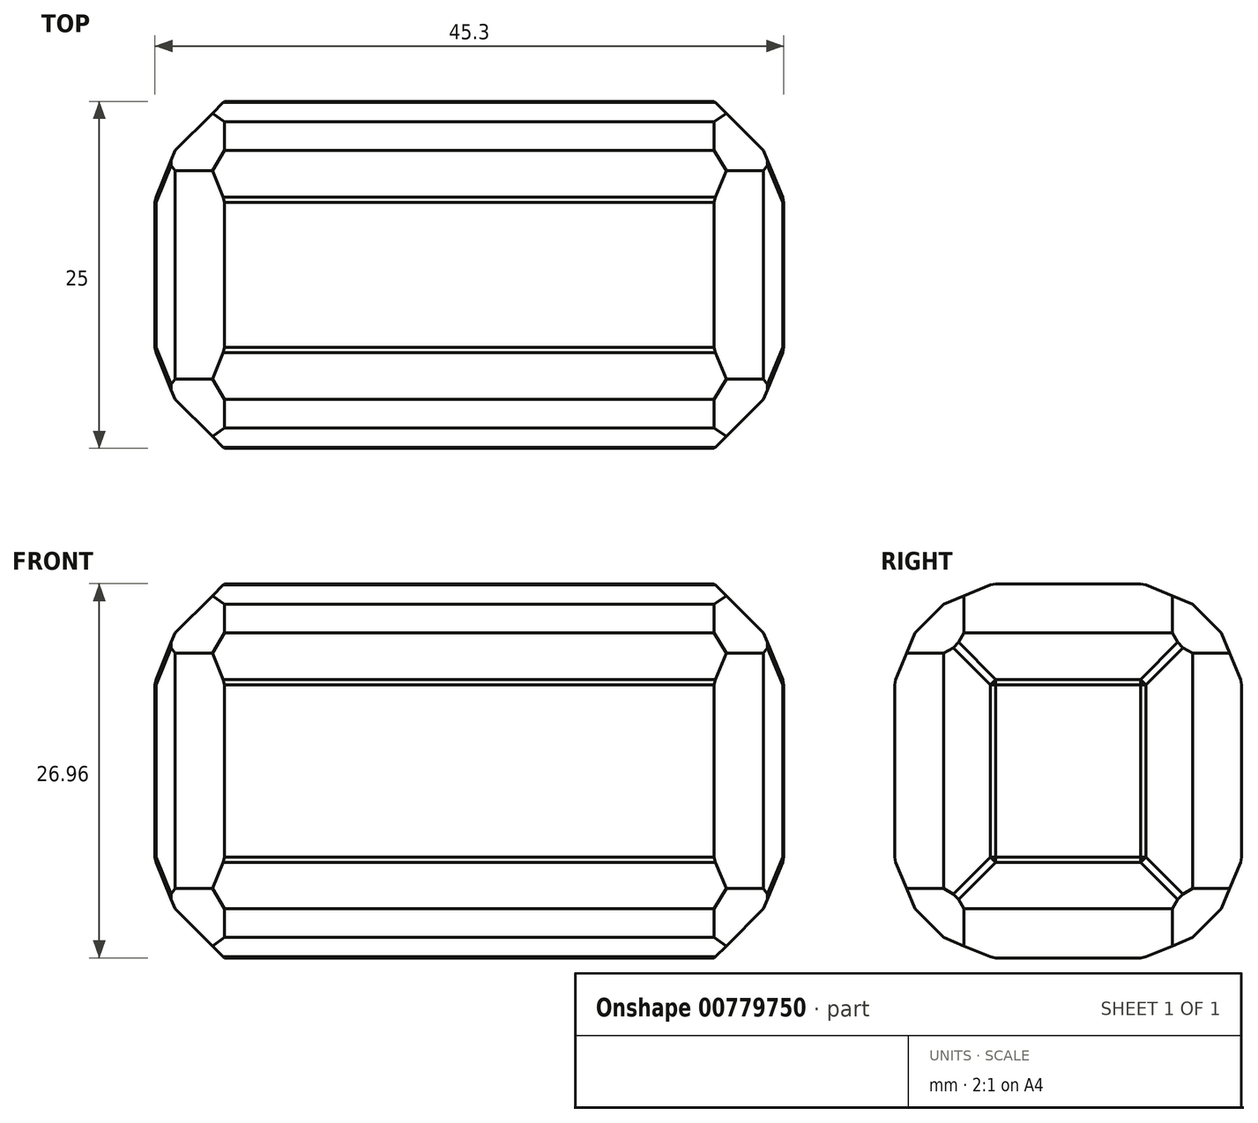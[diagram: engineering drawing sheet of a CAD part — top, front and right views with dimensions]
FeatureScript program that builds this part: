
annotation { "Feature Type Name" : "Feature", "Feature Type Description" : "" }
export const myFeature = defineFeature(function(context is Context, id is Id, definition is map)
    precondition{}
    {
        {
            var Q0;
            Q0=qCreatedBy(makeId("Front.planeOp"),FACE);
            var sketch = newSketch(context, id + "F0", { "sketchPlane" : qUnion([Q0])});
            skLineSegment(sketch, "E0", {"start": v(0, 0) * mm, "end": v(45.3, 0) * mm});
            skLineSegment(sketch, "E1", {"start": v(45.3, 0) * mm, "end": v(45.3, 26.96) * mm});
            skLineSegment(sketch, "E2", {"start": v(45.3, 26.96) * mm, "end": v(0, 26.96) * mm});
            skLineSegment(sketch, "E3", {"start": v(0, 0) * mm, "end": v(0, 26.96) * mm});
            skSolve(sketch);
        }
        {
            var Q0;
            Q0=makeQuery(id+"F0.imprint","IMPRINT",FACE,{"disambiguationData":[TD([[makeQuery(id+"F0.imprint","IMPRINT",EDGE,{"derivedFrom":sQuery(id+"F0.wireOp",EDGE,"E0")}),1.0]])]});
            extrude(context, id + "F1", {"entities" : qUnion([Q0]), "depth" : 25 * mm, "offsetDistance" : 25 * mm});
        }
        {
            var Q0;
            Q0=makeQuery(id+"F1.opExtrude","CAP_EDGE",EDGE,{"disambiguationData":[OSD([sQuery(id+"F0.wireOp",EDGE,"E2")])],"isStart":false});
            var Q1;
            Q1=makeQuery(id+"F1.opExtrude","SWEPT_EDGE",EDGE,{"disambiguationData":[OSD([sQuery(id+"F0.wireOp",EDGE,"E1"),sQuery(id+"F0.wireOp",EDGE,"E2")])]});
            var Q2;
            Q2=makeQuery(id+"F1.opExtrude","CAP_EDGE",EDGE,{"disambiguationData":[OSD([sQuery(id+"F0.wireOp",EDGE,"E2")])],"isStart":true});
            var Q3;
            Q3=makeQuery(id+"F1.opExtrude","SWEPT_EDGE",EDGE,{"disambiguationData":[OSD([sQuery(id+"F0.wireOp",EDGE,"E2"),sQuery(id+"F0.wireOp",EDGE,"E3")])]});
            var Q4;
            Q4=makeQuery(id+"F1.opExtrude","CAP_EDGE",EDGE,{"disambiguationData":[OSD([sQuery(id+"F0.wireOp",EDGE,"E0")])],"isStart":false});
            var Q5;
            Q5=makeQuery(id+"F1.opExtrude","CAP_EDGE",EDGE,{"disambiguationData":[OSD([sQuery(id+"F0.wireOp",EDGE,"E1")])],"isStart":false});
            var Q6;
            Q6=makeQuery(id+"F1.opExtrude","SWEPT_EDGE",EDGE,{"disambiguationData":[OSD([sQuery(id+"F0.wireOp",EDGE,"E0"),sQuery(id+"F0.wireOp",EDGE,"E1")])]});
            var Q7;
            Q7=makeQuery(id+"F1.opExtrude","CAP_EDGE",EDGE,{"disambiguationData":[OSD([sQuery(id+"F0.wireOp",EDGE,"E1")])],"isStart":true});
            var Q8;
            Q8=makeQuery(id+"F1.opExtrude","CAP_EDGE",EDGE,{"disambiguationData":[OSD([sQuery(id+"F0.wireOp",EDGE,"E3")])],"isStart":false});
            var Q9;
            Q9=makeQuery(id+"F1.opExtrude","CAP_EDGE",EDGE,{"disambiguationData":[OSD([sQuery(id+"F0.wireOp",EDGE,"E3")])],"isStart":true});
            var Q10;
            Q10=makeQuery(id+"F1.opExtrude","SWEPT_EDGE",EDGE,{"disambiguationData":[OSD([sQuery(id+"F0.wireOp",EDGE,"E0"),sQuery(id+"F0.wireOp",EDGE,"E3")])]});
            var Q11;
            Q11=makeQuery(id+"F1.opExtrude","CAP_EDGE",EDGE,{"disambiguationData":[OSD([sQuery(id+"F0.wireOp",EDGE,"E0")])],"isStart":true});
            chamfer(context, id + "F2", {"entities" : qUnion([Q0, Q1, Q2, Q3, Q4, Q5, Q6, Q7, Q8, Q9, Q10, Q11]), "width" : 5 * mm, "tangentPropagation" : true});
        }
        {
            var Q0;
            {var subQ0=sQuery(id+"F0.wireOp",EDGE,"E1");Q0=makeQuery(id+"F2.opChamfer","BLEND_EDGE",EDGE,{"blendedFrom":[makeQuery(id+"F1.opExtrude","SWEPT_EDGE",EDGE,{"disambiguationData":[OSD([subQ0,sQuery(id+"F0.wireOp",EDGE,"E2")])]}),makeQuery(id+"F1.opExtrude","SWEPT_FACE",FACE,{"disambiguationData":[OSD([subQ0])]})],"blendedInto":[makeQuery(id+"F1.opExtrude","SWEPT_FACE",FACE,{"disambiguationData":[OSD([subQ0])]})]});}
            var Q1;
            {var subQ0=sQuery(id+"F0.wireOp",EDGE,"E1");Q1=makeQuery(id+"F2.opChamfer","BLEND_EDGE",EDGE,{"blendedFrom":[makeQuery(id+"F1.opExtrude","CAP_EDGE",EDGE,{"disambiguationData":[OSD([subQ0])],"isStart":false}),makeQuery(id+"F1.opExtrude","SWEPT_FACE",FACE,{"disambiguationData":[OSD([subQ0])]})],"blendedInto":[makeQuery(id+"F1.opExtrude","SWEPT_FACE",FACE,{"disambiguationData":[OSD([subQ0])]})]});}
            var Q2;
            {var subQ0=sQuery(id+"F0.wireOp",EDGE,"E1");Q2=makeQuery(id+"F2.opChamfer","BLEND_EDGE",EDGE,{"blendedFrom":[makeQuery(id+"F1.opExtrude","SWEPT_EDGE",EDGE,{"disambiguationData":[OSD([sQuery(id+"F0.wireOp",EDGE,"E0"),subQ0])]}),makeQuery(id+"F1.opExtrude","SWEPT_FACE",FACE,{"disambiguationData":[OSD([subQ0])]})],"blendedInto":[makeQuery(id+"F1.opExtrude","SWEPT_FACE",FACE,{"disambiguationData":[OSD([subQ0])]})]});}
            var Q3;
            {var subQ0=sQuery(id+"F0.wireOp",EDGE,"E1");Q3=makeQuery(id+"F2.opChamfer","BLEND_EDGE",EDGE,{"blendedFrom":[makeQuery(id+"F1.opExtrude","CAP_EDGE",EDGE,{"disambiguationData":[OSD([subQ0])],"isStart":true}),makeQuery(id+"F1.opExtrude","SWEPT_FACE",FACE,{"disambiguationData":[OSD([subQ0])]})],"blendedInto":[makeQuery(id+"F1.opExtrude","SWEPT_FACE",FACE,{"disambiguationData":[OSD([subQ0])]})]});}
            var Q4;
            {var subQ0=sQuery(id+"F0.wireOp",EDGE,"E3");Q4=makeQuery(id+"F2.opChamfer","BLEND_EDGE",EDGE,{"blendedFrom":[makeQuery(id+"F1.opExtrude","CAP_EDGE",EDGE,{"disambiguationData":[OSD([subQ0])],"isStart":true}),makeQuery(id+"F1.opExtrude","SWEPT_FACE",FACE,{"disambiguationData":[OSD([subQ0])]})],"blendedInto":[makeQuery(id+"F1.opExtrude","SWEPT_FACE",FACE,{"disambiguationData":[OSD([subQ0])]})]});}
            var Q5;
            {var subQ0=sQuery(id+"F0.wireOp",EDGE,"E3");Q5=makeQuery(id+"F2.opChamfer","BLEND_EDGE",EDGE,{"blendedFrom":[makeQuery(id+"F1.opExtrude","SWEPT_EDGE",EDGE,{"disambiguationData":[OSD([sQuery(id+"F0.wireOp",EDGE,"E2"),subQ0])]}),makeQuery(id+"F1.opExtrude","SWEPT_FACE",FACE,{"disambiguationData":[OSD([subQ0])]})],"blendedInto":[makeQuery(id+"F1.opExtrude","SWEPT_FACE",FACE,{"disambiguationData":[OSD([subQ0])]})]});}
            var Q6;
            {var subQ0=sQuery(id+"F0.wireOp",EDGE,"E3");Q6=makeQuery(id+"F2.opChamfer","BLEND_EDGE",EDGE,{"blendedFrom":[makeQuery(id+"F1.opExtrude","CAP_EDGE",EDGE,{"disambiguationData":[OSD([subQ0])],"isStart":false}),makeQuery(id+"F1.opExtrude","SWEPT_FACE",FACE,{"disambiguationData":[OSD([subQ0])]})],"blendedInto":[makeQuery(id+"F1.opExtrude","SWEPT_FACE",FACE,{"disambiguationData":[OSD([subQ0])]})]});}
            var Q7;
            {var subQ0=sQuery(id+"F0.wireOp",EDGE,"E3");Q7=makeQuery(id+"F2.opChamfer","BLEND_EDGE",EDGE,{"blendedFrom":[makeQuery(id+"F1.opExtrude","SWEPT_EDGE",EDGE,{"disambiguationData":[OSD([sQuery(id+"F0.wireOp",EDGE,"E0"),subQ0])]}),makeQuery(id+"F1.opExtrude","SWEPT_FACE",FACE,{"disambiguationData":[OSD([subQ0])]})],"blendedInto":[makeQuery(id+"F1.opExtrude","SWEPT_FACE",FACE,{"disambiguationData":[OSD([subQ0])]})]});}
            chamfer(context, id + "F3", {"entities" : qUnion([Q0, Q1, Q2, Q3, Q4, Q5, Q6, Q7]), "width" : 5 * mm, "tangentPropagation" : true});
        }
        {
            var Q0;
            {var subQ0=sQuery(id+"F0.wireOp",EDGE,"E0");Q0=makeQuery(id+"F2.opChamfer","BLEND_EDGE",EDGE,{"blendedFrom":[makeQuery(id+"F1.opExtrude","CAP_EDGE",EDGE,{"disambiguationData":[OSD([subQ0])],"isStart":true}),makeQuery(id+"F1.opExtrude","CAP_FACE",FACE,{"disambiguationData":[OSD([subQ0,sQuery(id+"F0.wireOp",EDGE,"E1"),sQuery(id+"F0.wireOp",EDGE,"E2"),sQuery(id+"F0.wireOp",EDGE,"E3")])],"isStart":true})],"blendedInto":[makeQuery(id+"F1.opExtrude","CAP_FACE",FACE,{"disambiguationData":[OSD([subQ0,sQuery(id+"F0.wireOp",EDGE,"E1"),sQuery(id+"F0.wireOp",EDGE,"E2"),sQuery(id+"F0.wireOp",EDGE,"E3")])],"isStart":true})]});}
            var Q1;
            {var subQ0=sQuery(id+"F0.wireOp",EDGE,"E0");Q1=makeQuery(id+"F2.opChamfer","BLEND_EDGE",EDGE,{"blendedFrom":[makeQuery(id+"F1.opExtrude","CAP_EDGE",EDGE,{"disambiguationData":[OSD([subQ0])],"isStart":true}),makeQuery(id+"F1.opExtrude","SWEPT_FACE",FACE,{"disambiguationData":[OSD([subQ0])]})],"blendedInto":[makeQuery(id+"F1.opExtrude","SWEPT_FACE",FACE,{"disambiguationData":[OSD([subQ0])]})]});}
            var Q2;
            {var subQ0=sQuery(id+"F0.wireOp",EDGE,"E2");Q2=makeQuery(id+"F2.opChamfer","BLEND_EDGE",EDGE,{"blendedFrom":[makeQuery(id+"F1.opExtrude","CAP_EDGE",EDGE,{"disambiguationData":[OSD([subQ0])],"isStart":false}),makeQuery(id+"F1.opExtrude","SWEPT_FACE",FACE,{"disambiguationData":[OSD([subQ0])]})],"blendedInto":[makeQuery(id+"F1.opExtrude","SWEPT_FACE",FACE,{"disambiguationData":[OSD([subQ0])]})]});}
            var Q3;
            {var subQ0=sQuery(id+"F0.wireOp",EDGE,"E2");Q3=makeQuery(id+"F2.opChamfer","BLEND_EDGE",EDGE,{"blendedFrom":[makeQuery(id+"F1.opExtrude","CAP_EDGE",EDGE,{"disambiguationData":[OSD([subQ0])],"isStart":false}),makeQuery(id+"F1.opExtrude","CAP_FACE",FACE,{"disambiguationData":[OSD([sQuery(id+"F0.wireOp",EDGE,"E0"),sQuery(id+"F0.wireOp",EDGE,"E1"),subQ0,sQuery(id+"F0.wireOp",EDGE,"E3")])],"isStart":false})],"blendedInto":[makeQuery(id+"F1.opExtrude","CAP_FACE",FACE,{"disambiguationData":[OSD([sQuery(id+"F0.wireOp",EDGE,"E0"),sQuery(id+"F0.wireOp",EDGE,"E1"),subQ0,sQuery(id+"F0.wireOp",EDGE,"E3")])],"isStart":false})]});}
            var Q4;
            {var subQ0=sQuery(id+"F0.wireOp",EDGE,"E2");Q4=makeQuery(id+"F2.opChamfer","BLEND_EDGE",EDGE,{"blendedFrom":[makeQuery(id+"F1.opExtrude","CAP_EDGE",EDGE,{"disambiguationData":[OSD([subQ0])],"isStart":true}),makeQuery(id+"F1.opExtrude","SWEPT_FACE",FACE,{"disambiguationData":[OSD([subQ0])]})],"blendedInto":[makeQuery(id+"F1.opExtrude","SWEPT_FACE",FACE,{"disambiguationData":[OSD([subQ0])]})]});}
            var Q5;
            {var subQ0=sQuery(id+"F0.wireOp",EDGE,"E2");Q5=makeQuery(id+"F2.opChamfer","BLEND_EDGE",EDGE,{"blendedFrom":[makeQuery(id+"F1.opExtrude","CAP_EDGE",EDGE,{"disambiguationData":[OSD([subQ0])],"isStart":true}),makeQuery(id+"F1.opExtrude","CAP_FACE",FACE,{"disambiguationData":[OSD([sQuery(id+"F0.wireOp",EDGE,"E0"),sQuery(id+"F0.wireOp",EDGE,"E1"),subQ0,sQuery(id+"F0.wireOp",EDGE,"E3")])],"isStart":true})],"blendedInto":[makeQuery(id+"F1.opExtrude","CAP_FACE",FACE,{"disambiguationData":[OSD([sQuery(id+"F0.wireOp",EDGE,"E0"),sQuery(id+"F0.wireOp",EDGE,"E1"),subQ0,sQuery(id+"F0.wireOp",EDGE,"E3")])],"isStart":true})]});}
            var Q6;
            {var subQ0=sQuery(id+"F0.wireOp",EDGE,"E0");Q6=makeQuery(id+"F2.opChamfer","BLEND_EDGE",EDGE,{"blendedFrom":[makeQuery(id+"F1.opExtrude","CAP_EDGE",EDGE,{"disambiguationData":[OSD([subQ0])],"isStart":false}),makeQuery(id+"F1.opExtrude","SWEPT_FACE",FACE,{"disambiguationData":[OSD([subQ0])]})],"blendedInto":[makeQuery(id+"F1.opExtrude","SWEPT_FACE",FACE,{"disambiguationData":[OSD([subQ0])]})]});}
            var Q7;
            {var subQ0=sQuery(id+"F0.wireOp",EDGE,"E0");Q7=makeQuery(id+"F2.opChamfer","BLEND_EDGE",EDGE,{"blendedFrom":[makeQuery(id+"F1.opExtrude","CAP_EDGE",EDGE,{"disambiguationData":[OSD([subQ0])],"isStart":false}),makeQuery(id+"F1.opExtrude","CAP_FACE",FACE,{"disambiguationData":[OSD([subQ0,sQuery(id+"F0.wireOp",EDGE,"E1"),sQuery(id+"F0.wireOp",EDGE,"E2"),sQuery(id+"F0.wireOp",EDGE,"E3")])],"isStart":false})],"blendedInto":[makeQuery(id+"F1.opExtrude","CAP_FACE",FACE,{"disambiguationData":[OSD([subQ0,sQuery(id+"F0.wireOp",EDGE,"E1"),sQuery(id+"F0.wireOp",EDGE,"E2"),sQuery(id+"F0.wireOp",EDGE,"E3")])],"isStart":false})]});}
            chamfer(context, id + "F4", {"entities" : qUnion([Q0, Q1, Q2, Q3, Q4, Q5, Q6, Q7]), "width" : 5 * mm, "tangentPropagation" : true});
        }
        {
            var Q0;
            {var subQ0=sQuery(id+"F0.wireOp",EDGE,"E1");var subQ1=makeQuery(id+"F1.opExtrude","SWEPT_FACE",FACE,{"disambiguationData":[OSD([subQ0])]});Q0=makeQuery(id+"F3.opChamfer","BLEND_EDGE",EDGE,{"blendedFrom":[makeQuery(id+"F2.opChamfer","BLEND_EDGE",EDGE,{"blendedFrom":[makeQuery(id+"F1.opExtrude","SWEPT_EDGE",EDGE,{"disambiguationData":[OSD([subQ0,sQuery(id+"F0.wireOp",EDGE,"E2")])]}),subQ1],"blendedInto":[subQ1]}),makeQuery(id+"F2.opChamfer","BLEND_EDGE",EDGE,{"blendedFrom":[makeQuery(id+"F1.opExtrude","CAP_EDGE",EDGE,{"disambiguationData":[OSD([subQ0])],"isStart":true}),subQ1],"blendedInto":[subQ1]})],"blendedInto":[]});}
            var Q1;
            {var subQ0=sQuery(id+"F0.wireOp",EDGE,"E1");var subQ1=makeQuery(id+"F1.opExtrude","SWEPT_FACE",FACE,{"disambiguationData":[OSD([subQ0])]});Q1=makeQuery(id+"F3.opChamfer","BLEND_EDGE",EDGE,{"blendedFrom":[makeQuery(id+"F2.opChamfer","BLEND_EDGE",EDGE,{"blendedFrom":[makeQuery(id+"F1.opExtrude","SWEPT_EDGE",EDGE,{"disambiguationData":[OSD([sQuery(id+"F0.wireOp",EDGE,"E0"),subQ0])]}),subQ1],"blendedInto":[subQ1]}),makeQuery(id+"F2.opChamfer","BLEND_EDGE",EDGE,{"blendedFrom":[makeQuery(id+"F1.opExtrude","CAP_EDGE",EDGE,{"disambiguationData":[OSD([subQ0])],"isStart":true}),subQ1],"blendedInto":[subQ1]})],"blendedInto":[]});}
            var Q2;
            {var subQ0=sQuery(id+"F0.wireOp",EDGE,"E1");var subQ1=makeQuery(id+"F1.opExtrude","SWEPT_FACE",FACE,{"disambiguationData":[OSD([subQ0])]});Q2=makeQuery(id+"F3.opChamfer","BLEND_EDGE",EDGE,{"blendedFrom":[makeQuery(id+"F2.opChamfer","BLEND_EDGE",EDGE,{"blendedFrom":[makeQuery(id+"F1.opExtrude","SWEPT_EDGE",EDGE,{"disambiguationData":[OSD([sQuery(id+"F0.wireOp",EDGE,"E0"),subQ0])]}),subQ1],"blendedInto":[subQ1]}),makeQuery(id+"F2.opChamfer","BLEND_EDGE",EDGE,{"blendedFrom":[makeQuery(id+"F1.opExtrude","CAP_EDGE",EDGE,{"disambiguationData":[OSD([subQ0])],"isStart":false}),subQ1],"blendedInto":[subQ1]})],"blendedInto":[]});}
            var Q3;
            {var subQ0=sQuery(id+"F0.wireOp",EDGE,"E1");var subQ1=makeQuery(id+"F1.opExtrude","SWEPT_FACE",FACE,{"disambiguationData":[OSD([subQ0])]});Q3=makeQuery(id+"F3.opChamfer","BLEND_EDGE",EDGE,{"blendedFrom":[makeQuery(id+"F2.opChamfer","BLEND_EDGE",EDGE,{"blendedFrom":[makeQuery(id+"F1.opExtrude","SWEPT_EDGE",EDGE,{"disambiguationData":[OSD([subQ0,sQuery(id+"F0.wireOp",EDGE,"E2")])]}),subQ1],"blendedInto":[subQ1]}),makeQuery(id+"F2.opChamfer","BLEND_EDGE",EDGE,{"blendedFrom":[makeQuery(id+"F1.opExtrude","CAP_EDGE",EDGE,{"disambiguationData":[OSD([subQ0])],"isStart":false}),subQ1],"blendedInto":[subQ1]})],"blendedInto":[]});}
            var Q4;
            {var subQ0=sQuery(id+"F0.wireOp",EDGE,"E1");var subQ1=makeQuery(id+"F1.opExtrude","SWEPT_FACE",FACE,{"disambiguationData":[OSD([subQ0])]});Q4=makeQuery(id+"F3.opChamfer","BLEND_EDGE",EDGE,{"blendedFrom":[makeQuery(id+"F2.opChamfer","BLEND_EDGE",EDGE,{"blendedFrom":[makeQuery(id+"F1.opExtrude","CAP_EDGE",EDGE,{"disambiguationData":[OSD([subQ0])],"isStart":false}),subQ1],"blendedInto":[subQ1]}),subQ1],"blendedInto":[subQ1]});}
            var Q5;
            {var subQ0=sQuery(id+"F0.wireOp",EDGE,"E1");var subQ1=makeQuery(id+"F1.opExtrude","SWEPT_FACE",FACE,{"disambiguationData":[OSD([subQ0])]});Q5=makeQuery(id+"F3.opChamfer","BLEND_EDGE",EDGE,{"blendedFrom":[makeQuery(id+"F2.opChamfer","BLEND_EDGE",EDGE,{"blendedFrom":[makeQuery(id+"F1.opExtrude","SWEPT_EDGE",EDGE,{"disambiguationData":[OSD([subQ0,sQuery(id+"F0.wireOp",EDGE,"E2")])]}),subQ1],"blendedInto":[subQ1]}),subQ1],"blendedInto":[subQ1]});}
            var Q6;
            {var subQ0=sQuery(id+"F0.wireOp",EDGE,"E1");var subQ1=makeQuery(id+"F1.opExtrude","SWEPT_FACE",FACE,{"disambiguationData":[OSD([subQ0])]});Q6=makeQuery(id+"F3.opChamfer","BLEND_EDGE",EDGE,{"blendedFrom":[makeQuery(id+"F2.opChamfer","BLEND_EDGE",EDGE,{"blendedFrom":[makeQuery(id+"F1.opExtrude","CAP_EDGE",EDGE,{"disambiguationData":[OSD([subQ0])],"isStart":true}),subQ1],"blendedInto":[subQ1]}),subQ1],"blendedInto":[subQ1]});}
            var Q7;
            {var subQ0=sQuery(id+"F0.wireOp",EDGE,"E1");var subQ1=makeQuery(id+"F1.opExtrude","SWEPT_FACE",FACE,{"disambiguationData":[OSD([subQ0])]});Q7=makeQuery(id+"F3.opChamfer","BLEND_EDGE",EDGE,{"blendedFrom":[makeQuery(id+"F2.opChamfer","BLEND_EDGE",EDGE,{"blendedFrom":[makeQuery(id+"F1.opExtrude","SWEPT_EDGE",EDGE,{"disambiguationData":[OSD([sQuery(id+"F0.wireOp",EDGE,"E0"),subQ0])]}),subQ1],"blendedInto":[subQ1]}),subQ1],"blendedInto":[subQ1]});}
            var Q8;
            {var subQ0=sQuery(id+"F0.wireOp",EDGE,"E3");var subQ1=makeQuery(id+"F1.opExtrude","SWEPT_FACE",FACE,{"disambiguationData":[OSD([subQ0])]});Q8=makeQuery(id+"F3.opChamfer","BLEND_EDGE",EDGE,{"blendedFrom":[makeQuery(id+"F2.opChamfer","BLEND_EDGE",EDGE,{"blendedFrom":[makeQuery(id+"F1.opExtrude","SWEPT_EDGE",EDGE,{"disambiguationData":[OSD([sQuery(id+"F0.wireOp",EDGE,"E0"),subQ0])]}),subQ1],"blendedInto":[subQ1]}),makeQuery(id+"F2.opChamfer","BLEND_EDGE",EDGE,{"blendedFrom":[makeQuery(id+"F1.opExtrude","CAP_EDGE",EDGE,{"disambiguationData":[OSD([subQ0])],"isStart":false}),subQ1],"blendedInto":[subQ1]})],"blendedInto":[]});}
            var Q9;
            {var subQ0=sQuery(id+"F0.wireOp",EDGE,"E3");var subQ1=makeQuery(id+"F1.opExtrude","SWEPT_FACE",FACE,{"disambiguationData":[OSD([subQ0])]});Q9=makeQuery(id+"F3.opChamfer","BLEND_EDGE",EDGE,{"blendedFrom":[makeQuery(id+"F2.opChamfer","BLEND_EDGE",EDGE,{"blendedFrom":[makeQuery(id+"F1.opExtrude","SWEPT_EDGE",EDGE,{"disambiguationData":[OSD([sQuery(id+"F0.wireOp",EDGE,"E0"),subQ0])]}),subQ1],"blendedInto":[subQ1]}),makeQuery(id+"F2.opChamfer","BLEND_EDGE",EDGE,{"blendedFrom":[makeQuery(id+"F1.opExtrude","CAP_EDGE",EDGE,{"disambiguationData":[OSD([subQ0])],"isStart":true}),subQ1],"blendedInto":[subQ1]})],"blendedInto":[]});}
            var Q10;
            {var subQ0=sQuery(id+"F0.wireOp",EDGE,"E3");var subQ1=makeQuery(id+"F1.opExtrude","SWEPT_FACE",FACE,{"disambiguationData":[OSD([subQ0])]});Q10=makeQuery(id+"F3.opChamfer","BLEND_EDGE",EDGE,{"blendedFrom":[makeQuery(id+"F2.opChamfer","BLEND_EDGE",EDGE,{"blendedFrom":[makeQuery(id+"F1.opExtrude","SWEPT_EDGE",EDGE,{"disambiguationData":[OSD([sQuery(id+"F0.wireOp",EDGE,"E2"),subQ0])]}),subQ1],"blendedInto":[subQ1]}),makeQuery(id+"F2.opChamfer","BLEND_EDGE",EDGE,{"blendedFrom":[makeQuery(id+"F1.opExtrude","CAP_EDGE",EDGE,{"disambiguationData":[OSD([subQ0])],"isStart":true}),subQ1],"blendedInto":[subQ1]})],"blendedInto":[]});}
            var Q11;
            {var subQ0=sQuery(id+"F0.wireOp",EDGE,"E3");var subQ1=makeQuery(id+"F1.opExtrude","SWEPT_FACE",FACE,{"disambiguationData":[OSD([subQ0])]});Q11=makeQuery(id+"F3.opChamfer","BLEND_EDGE",EDGE,{"blendedFrom":[makeQuery(id+"F2.opChamfer","BLEND_EDGE",EDGE,{"blendedFrom":[makeQuery(id+"F1.opExtrude","SWEPT_EDGE",EDGE,{"disambiguationData":[OSD([sQuery(id+"F0.wireOp",EDGE,"E2"),subQ0])]}),subQ1],"blendedInto":[subQ1]}),makeQuery(id+"F2.opChamfer","BLEND_EDGE",EDGE,{"blendedFrom":[makeQuery(id+"F1.opExtrude","CAP_EDGE",EDGE,{"disambiguationData":[OSD([subQ0])],"isStart":false}),subQ1],"blendedInto":[subQ1]})],"blendedInto":[]});}
            var Q12;
            {var subQ0=sQuery(id+"F0.wireOp",EDGE,"E3");var subQ1=makeQuery(id+"F1.opExtrude","SWEPT_FACE",FACE,{"disambiguationData":[OSD([subQ0])]});Q12=makeQuery(id+"F3.opChamfer","BLEND_EDGE",EDGE,{"blendedFrom":[makeQuery(id+"F2.opChamfer","BLEND_EDGE",EDGE,{"blendedFrom":[makeQuery(id+"F1.opExtrude","SWEPT_EDGE",EDGE,{"disambiguationData":[OSD([sQuery(id+"F0.wireOp",EDGE,"E2"),subQ0])]}),subQ1],"blendedInto":[subQ1]}),subQ1],"blendedInto":[subQ1]});}
            var Q13;
            {var subQ0=sQuery(id+"F0.wireOp",EDGE,"E3");var subQ1=makeQuery(id+"F1.opExtrude","SWEPT_FACE",FACE,{"disambiguationData":[OSD([subQ0])]});Q13=makeQuery(id+"F3.opChamfer","BLEND_EDGE",EDGE,{"blendedFrom":[makeQuery(id+"F2.opChamfer","BLEND_EDGE",EDGE,{"blendedFrom":[makeQuery(id+"F1.opExtrude","SWEPT_EDGE",EDGE,{"disambiguationData":[OSD([sQuery(id+"F0.wireOp",EDGE,"E0"),subQ0])]}),subQ1],"blendedInto":[subQ1]}),subQ1],"blendedInto":[subQ1]});}
            var Q14;
            {var subQ0=sQuery(id+"F0.wireOp",EDGE,"E3");var subQ1=makeQuery(id+"F1.opExtrude","SWEPT_FACE",FACE,{"disambiguationData":[OSD([subQ0])]});Q14=makeQuery(id+"F3.opChamfer","BLEND_EDGE",EDGE,{"blendedFrom":[makeQuery(id+"F2.opChamfer","BLEND_EDGE",EDGE,{"blendedFrom":[makeQuery(id+"F1.opExtrude","CAP_EDGE",EDGE,{"disambiguationData":[OSD([subQ0])],"isStart":false}),subQ1],"blendedInto":[subQ1]}),subQ1],"blendedInto":[subQ1]});}
            var Q15;
            {var subQ0=sQuery(id+"F0.wireOp",EDGE,"E3");var subQ1=makeQuery(id+"F1.opExtrude","SWEPT_FACE",FACE,{"disambiguationData":[OSD([subQ0])]});Q15=makeQuery(id+"F3.opChamfer","BLEND_EDGE",EDGE,{"blendedFrom":[makeQuery(id+"F2.opChamfer","BLEND_EDGE",EDGE,{"blendedFrom":[makeQuery(id+"F1.opExtrude","CAP_EDGE",EDGE,{"disambiguationData":[OSD([subQ0])],"isStart":true}),subQ1],"blendedInto":[subQ1]}),subQ1],"blendedInto":[subQ1]});}
            chamfer(context, id + "F5", {"entities" : qUnion([Q0, Q1, Q2, Q3, Q4, Q5, Q6, Q7, Q8, Q9, Q10, Q11, Q12, Q13, Q14, Q15]), "width" : 1 * mm, "tangentPropagation" : true});
        }
        {
            var Q0;
            {var subQ0=sQuery(id+"F0.wireOp",EDGE,"E0");var subQ1=makeQuery(id+"F1.opExtrude","SWEPT_FACE",FACE,{"disambiguationData":[OSD([subQ0])]});Q0=makeQuery(id+"F4.opChamfer","BLEND_EDGE",EDGE,{"blendedFrom":[makeQuery(id+"F2.opChamfer","BLEND_EDGE",EDGE,{"blendedFrom":[makeQuery(id+"F1.opExtrude","CAP_EDGE",EDGE,{"disambiguationData":[OSD([subQ0])],"isStart":false}),subQ1],"blendedInto":[subQ1]}),subQ1],"blendedInto":[subQ1]});}
            var Q1;
            {var subQ0=sQuery(id+"F0.wireOp",EDGE,"E0");var subQ1=makeQuery(id+"F1.opExtrude","SWEPT_FACE",FACE,{"disambiguationData":[OSD([subQ0])]});Q1=makeQuery(id+"F4.opChamfer","BLEND_EDGE",EDGE,{"blendedFrom":[makeQuery(id+"F2.opChamfer","BLEND_EDGE",EDGE,{"blendedFrom":[makeQuery(id+"F1.opExtrude","CAP_EDGE",EDGE,{"disambiguationData":[OSD([subQ0])],"isStart":true}),subQ1],"blendedInto":[subQ1]}),subQ1],"blendedInto":[subQ1]});}
            var Q2;
            {var subQ0=sQuery(id+"F0.wireOp",EDGE,"E0");var subQ1=makeQuery(id+"F1.opExtrude","CAP_EDGE",EDGE,{"disambiguationData":[OSD([subQ0])],"isStart":true});Q2=makeQuery(id+"F4.opChamfer","BLEND_EDGE",EDGE,{"blendedFrom":[makeQuery(id+"F2.opChamfer","BLEND_EDGE",EDGE,{"blendedFrom":[subQ1,makeQuery(id+"F1.opExtrude","SWEPT_FACE",FACE,{"disambiguationData":[OSD([subQ0])]})],"blendedInto":[makeQuery(id+"F1.opExtrude","SWEPT_FACE",FACE,{"disambiguationData":[OSD([subQ0])]})]}),makeQuery(id+"F2.opChamfer","BLEND_EDGE",EDGE,{"blendedFrom":[subQ1,makeQuery(id+"F1.opExtrude","CAP_FACE",FACE,{"disambiguationData":[OSD([subQ0,sQuery(id+"F0.wireOp",EDGE,"E1"),sQuery(id+"F0.wireOp",EDGE,"E2"),sQuery(id+"F0.wireOp",EDGE,"E3")])],"isStart":true})],"blendedInto":[makeQuery(id+"F1.opExtrude","CAP_FACE",FACE,{"disambiguationData":[OSD([subQ0,sQuery(id+"F0.wireOp",EDGE,"E1"),sQuery(id+"F0.wireOp",EDGE,"E2"),sQuery(id+"F0.wireOp",EDGE,"E3")])],"isStart":true})]})],"blendedInto":[]});}
            var Q3;
            {var subQ0=sQuery(id+"F0.wireOp",EDGE,"E2");var subQ1=makeQuery(id+"F1.opExtrude","CAP_FACE",FACE,{"disambiguationData":[OSD([sQuery(id+"F0.wireOp",EDGE,"E0"),sQuery(id+"F0.wireOp",EDGE,"E1"),subQ0,sQuery(id+"F0.wireOp",EDGE,"E3")])],"isStart":true});Q3=makeQuery(id+"F4.opChamfer","BLEND_EDGE",EDGE,{"blendedFrom":[makeQuery(id+"F2.opChamfer","BLEND_EDGE",EDGE,{"blendedFrom":[makeQuery(id+"F1.opExtrude","CAP_EDGE",EDGE,{"disambiguationData":[OSD([subQ0])],"isStart":true}),subQ1],"blendedInto":[subQ1]}),subQ1],"blendedInto":[subQ1]});}
            var Q4;
            {var subQ0=sQuery(id+"F0.wireOp",EDGE,"E0");var subQ1=makeQuery(id+"F1.opExtrude","CAP_FACE",FACE,{"disambiguationData":[OSD([subQ0,sQuery(id+"F0.wireOp",EDGE,"E1"),sQuery(id+"F0.wireOp",EDGE,"E2"),sQuery(id+"F0.wireOp",EDGE,"E3")])],"isStart":true});Q4=makeQuery(id+"F4.opChamfer","BLEND_EDGE",EDGE,{"blendedFrom":[makeQuery(id+"F2.opChamfer","BLEND_EDGE",EDGE,{"blendedFrom":[makeQuery(id+"F1.opExtrude","CAP_EDGE",EDGE,{"disambiguationData":[OSD([subQ0])],"isStart":true}),subQ1],"blendedInto":[subQ1]}),subQ1],"blendedInto":[subQ1]});}
            var Q5;
            {var subQ0=sQuery(id+"F0.wireOp",EDGE,"E2");var subQ1=makeQuery(id+"F1.opExtrude","CAP_EDGE",EDGE,{"disambiguationData":[OSD([subQ0])],"isStart":true});Q5=makeQuery(id+"F4.opChamfer","BLEND_EDGE",EDGE,{"blendedFrom":[makeQuery(id+"F2.opChamfer","BLEND_EDGE",EDGE,{"blendedFrom":[subQ1,makeQuery(id+"F1.opExtrude","CAP_FACE",FACE,{"disambiguationData":[OSD([sQuery(id+"F0.wireOp",EDGE,"E0"),sQuery(id+"F0.wireOp",EDGE,"E1"),subQ0,sQuery(id+"F0.wireOp",EDGE,"E3")])],"isStart":true})],"blendedInto":[makeQuery(id+"F1.opExtrude","CAP_FACE",FACE,{"disambiguationData":[OSD([sQuery(id+"F0.wireOp",EDGE,"E0"),sQuery(id+"F0.wireOp",EDGE,"E1"),subQ0,sQuery(id+"F0.wireOp",EDGE,"E3")])],"isStart":true})]}),makeQuery(id+"F2.opChamfer","BLEND_EDGE",EDGE,{"blendedFrom":[subQ1,makeQuery(id+"F1.opExtrude","SWEPT_FACE",FACE,{"disambiguationData":[OSD([subQ0])]})],"blendedInto":[makeQuery(id+"F1.opExtrude","SWEPT_FACE",FACE,{"disambiguationData":[OSD([subQ0])]})]})],"blendedInto":[]});}
            var Q6;
            {var subQ0=sQuery(id+"F0.wireOp",EDGE,"E2");var subQ1=makeQuery(id+"F1.opExtrude","SWEPT_FACE",FACE,{"disambiguationData":[OSD([subQ0])]});Q6=makeQuery(id+"F4.opChamfer","BLEND_EDGE",EDGE,{"blendedFrom":[makeQuery(id+"F2.opChamfer","BLEND_EDGE",EDGE,{"blendedFrom":[makeQuery(id+"F1.opExtrude","CAP_EDGE",EDGE,{"disambiguationData":[OSD([subQ0])],"isStart":true}),subQ1],"blendedInto":[subQ1]}),subQ1],"blendedInto":[subQ1]});}
            var Q7;
            {var subQ0=sQuery(id+"F0.wireOp",EDGE,"E2");var subQ1=makeQuery(id+"F1.opExtrude","SWEPT_FACE",FACE,{"disambiguationData":[OSD([subQ0])]});Q7=makeQuery(id+"F4.opChamfer","BLEND_EDGE",EDGE,{"blendedFrom":[makeQuery(id+"F2.opChamfer","BLEND_EDGE",EDGE,{"blendedFrom":[makeQuery(id+"F1.opExtrude","CAP_EDGE",EDGE,{"disambiguationData":[OSD([subQ0])],"isStart":false}),subQ1],"blendedInto":[subQ1]}),subQ1],"blendedInto":[subQ1]});}
            var Q8;
            {var subQ0=sQuery(id+"F0.wireOp",EDGE,"E2");var subQ1=makeQuery(id+"F1.opExtrude","CAP_EDGE",EDGE,{"disambiguationData":[OSD([subQ0])],"isStart":false});Q8=makeQuery(id+"F4.opChamfer","BLEND_EDGE",EDGE,{"blendedFrom":[makeQuery(id+"F2.opChamfer","BLEND_EDGE",EDGE,{"blendedFrom":[subQ1,makeQuery(id+"F1.opExtrude","CAP_FACE",FACE,{"disambiguationData":[OSD([sQuery(id+"F0.wireOp",EDGE,"E0"),sQuery(id+"F0.wireOp",EDGE,"E1"),subQ0,sQuery(id+"F0.wireOp",EDGE,"E3")])],"isStart":false})],"blendedInto":[makeQuery(id+"F1.opExtrude","CAP_FACE",FACE,{"disambiguationData":[OSD([sQuery(id+"F0.wireOp",EDGE,"E0"),sQuery(id+"F0.wireOp",EDGE,"E1"),subQ0,sQuery(id+"F0.wireOp",EDGE,"E3")])],"isStart":false})]}),makeQuery(id+"F2.opChamfer","BLEND_EDGE",EDGE,{"blendedFrom":[subQ1,makeQuery(id+"F1.opExtrude","SWEPT_FACE",FACE,{"disambiguationData":[OSD([subQ0])]})],"blendedInto":[makeQuery(id+"F1.opExtrude","SWEPT_FACE",FACE,{"disambiguationData":[OSD([subQ0])]})]})],"blendedInto":[]});}
            var Q9;
            {var subQ0=sQuery(id+"F0.wireOp",EDGE,"E2");var subQ1=makeQuery(id+"F1.opExtrude","CAP_FACE",FACE,{"disambiguationData":[OSD([sQuery(id+"F0.wireOp",EDGE,"E0"),sQuery(id+"F0.wireOp",EDGE,"E1"),subQ0,sQuery(id+"F0.wireOp",EDGE,"E3")])],"isStart":false});Q9=makeQuery(id+"F4.opChamfer","BLEND_EDGE",EDGE,{"blendedFrom":[makeQuery(id+"F2.opChamfer","BLEND_EDGE",EDGE,{"blendedFrom":[makeQuery(id+"F1.opExtrude","CAP_EDGE",EDGE,{"disambiguationData":[OSD([subQ0])],"isStart":false}),subQ1],"blendedInto":[subQ1]}),subQ1],"blendedInto":[subQ1]});}
            var Q10;
            {var subQ0=sQuery(id+"F0.wireOp",EDGE,"E0");var subQ1=makeQuery(id+"F1.opExtrude","CAP_FACE",FACE,{"disambiguationData":[OSD([subQ0,sQuery(id+"F0.wireOp",EDGE,"E1"),sQuery(id+"F0.wireOp",EDGE,"E2"),sQuery(id+"F0.wireOp",EDGE,"E3")])],"isStart":false});Q10=makeQuery(id+"F4.opChamfer","BLEND_EDGE",EDGE,{"blendedFrom":[makeQuery(id+"F2.opChamfer","BLEND_EDGE",EDGE,{"blendedFrom":[makeQuery(id+"F1.opExtrude","CAP_EDGE",EDGE,{"disambiguationData":[OSD([subQ0])],"isStart":false}),subQ1],"blendedInto":[subQ1]}),subQ1],"blendedInto":[subQ1]});}
            var Q11;
            {var subQ0=sQuery(id+"F0.wireOp",EDGE,"E0");var subQ1=makeQuery(id+"F1.opExtrude","CAP_EDGE",EDGE,{"disambiguationData":[OSD([subQ0])],"isStart":false});Q11=makeQuery(id+"F4.opChamfer","BLEND_EDGE",EDGE,{"blendedFrom":[makeQuery(id+"F2.opChamfer","BLEND_EDGE",EDGE,{"blendedFrom":[subQ1,makeQuery(id+"F1.opExtrude","SWEPT_FACE",FACE,{"disambiguationData":[OSD([subQ0])]})],"blendedInto":[makeQuery(id+"F1.opExtrude","SWEPT_FACE",FACE,{"disambiguationData":[OSD([subQ0])]})]}),makeQuery(id+"F2.opChamfer","BLEND_EDGE",EDGE,{"blendedFrom":[subQ1,makeQuery(id+"F1.opExtrude","CAP_FACE",FACE,{"disambiguationData":[OSD([subQ0,sQuery(id+"F0.wireOp",EDGE,"E1"),sQuery(id+"F0.wireOp",EDGE,"E2"),sQuery(id+"F0.wireOp",EDGE,"E3")])],"isStart":false})],"blendedInto":[makeQuery(id+"F1.opExtrude","CAP_FACE",FACE,{"disambiguationData":[OSD([subQ0,sQuery(id+"F0.wireOp",EDGE,"E1"),sQuery(id+"F0.wireOp",EDGE,"E2"),sQuery(id+"F0.wireOp",EDGE,"E3")])],"isStart":false})]})],"blendedInto":[]});}
            chamfer(context, id + "F6", {"entities" : qUnion([Q0, Q1, Q2, Q3, Q4, Q5, Q6, Q7, Q8, Q9, Q10, Q11]), "width" : 1 * mm, "tangentPropagation" : true});
        }
    });
